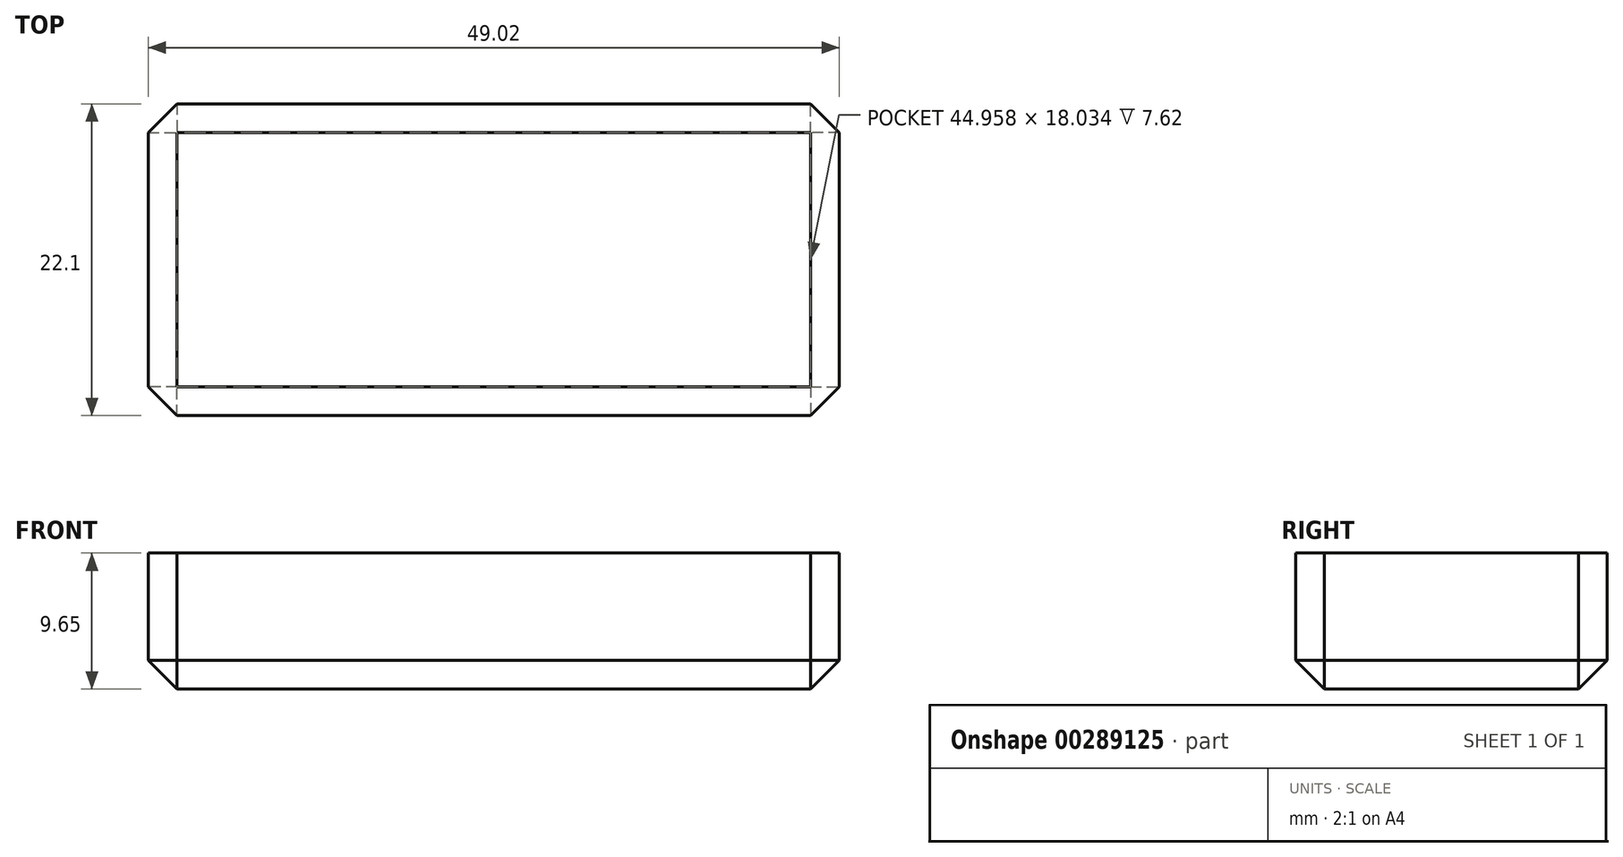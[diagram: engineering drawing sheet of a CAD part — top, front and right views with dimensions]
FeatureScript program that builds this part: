
annotation { "Feature Type Name" : "Feature", "Feature Type Description" : "" }
export const myFeature = defineFeature(function(context is Context, id is Id, definition is map)
    precondition{}
    {
        {
            var Q0;
            Q0=qCreatedBy(makeId("Top.planeOp"),FACE);
            var sketch = newSketch(context, id + "F0", { "sketchPlane" : qUnion([Q0])});
            skLineSegment(sketch, "E0.bottom", {"start": v(-24.51, 11.05) * mm, "end": v(24.51, 11.05) * mm});
            skLineSegment(sketch, "E0.top", {"start": v(-24.51, -11.05) * mm, "end": v(24.51, -11.05) * mm});
            skLineSegment(sketch, "E0.left", {"start": v(-24.51, 11.05) * mm, "end": v(-24.51, -11.05) * mm});
            skLineSegment(sketch, "E0.right", {"start": v(24.51, 11.05) * mm, "end": v(24.51, -11.05) * mm});
            skLineSegment(sketch, "E1", {"start": v(0, 0) * mm, "end": v(0, 11.05) * mm, "construction": true});
            skLineSegment(sketch, "E2", {"start": v(0, 0) * mm, "end": v(0, -11.05) * mm, "construction": true});
            skLineSegment(sketch, "E3", {"start": v(0, 0) * mm, "end": v(-24.51, 0) * mm, "construction": true});
            skPoint(sketch, "E3.endSnap0", {"position": v(-24.51, 0) * mm});
            skLineSegment(sketch, "E4", {"start": v(0, 0) * mm, "end": v(24.51, 0) * mm, "construction": true});
            skSolve(sketch);
        }
        {
            var Q0;
            Q0=makeQuery(id+"F0.imprint","IMPRINT",FACE,{"disambiguationData":[TD([[makeQuery(id+"F0.imprint","IMPRINT",EDGE,{"derivedFrom":sQuery(id+"F0.wireOp",EDGE,"E0.bottom")}),-1.0]])]});
            extrude(context, id + "F1", {"entities" : qUnion([Q0]), "depth" : 9.65 * mm});
        }
        {
            var Q0;
            Q0=makeQuery(id+"F1.opExtrude","CAP_FACE",FACE,{"disambiguationData":[OSD([sQuery(id+"F0.wireOp",EDGE,"E0.bottom"),sQuery(id+"F0.wireOp",EDGE,"E0.top"),sQuery(id+"F0.wireOp",EDGE,"E0.left"),sQuery(id+"F0.wireOp",EDGE,"E0.right")])],"isStart":false});
            var sketch = newSketch(context, id + "F2", { "sketchPlane" : qUnion([Q0])});
            skLineSegment(sketch, "E5.bottom", {"start": v(-22.48, 9.02) * mm, "end": v(22.48, 9.02) * mm});
            skLineSegment(sketch, "E5.top", {"start": v(-22.48, -9.02) * mm, "end": v(22.48, -9.02) * mm});
            skLineSegment(sketch, "E5.left", {"start": v(-22.48, 9.02) * mm, "end": v(-22.48, 4.29) * mm});
            skLineSegment(sketch, "E5.right", {"start": v(22.48, 9.02) * mm, "end": v(22.48, -9.02) * mm});
            skLineSegment(sketch, "E6", {"start": v(-22.48, 0) * mm, "end": v(-24.51, 0) * mm, "construction": true});
            skLineSegment(sketch, "E7", {"start": v(22.48, 0) * mm, "end": v(24.51, 0) * mm, "construction": true});
            skPoint(sketch, "E7.startSnap0", {"position": v(22.48, 0) * mm});
            skPoint(sketch, "E7.endSnap0", {"position": v(22.48, 0) * mm});
            skLineSegment(sketch, "E8", {"start": v(0, 9.02) * mm, "end": v(0, 11.05) * mm, "construction": true});
            skLineSegment(sketch, "E9", {"start": v(0, -9.02) * mm, "end": v(0, -11.05) * mm, "construction": true});
            skLineSegment(sketch, "E10.trimOffspring", {"start": v(-22.48, -4.29) * mm, "end": v(-22.48, -9.02) * mm});
            skLineSegment(sketch, "E11", {"start": v(-22.48, 4.29) * mm, "end": v(-22.48, -4.29) * mm});
            skSolve(sketch);
        }
        {
            var Q0;
            Q0=qSketchRegion(id+"F2",true);
            extrude(context, id + "F3", {"entities" : qUnion([Q0]), "operationType" : NewBodyOperationType.REMOVE, "oppositeDirection" : true, "depth" : 7.62 * mm});
        }
        {
            var Q0;
            Q0=makeQuery(id+"F1.opExtrude","CAP_EDGE",EDGE,{"disambiguationData":[OSD([sQuery(id+"F0.wireOp",EDGE,"E0.top")])],"isStart":true});
            var Q1;
            Q1=makeQuery(id+"F1.opExtrude","CAP_EDGE",EDGE,{"disambiguationData":[OSD([sQuery(id+"F0.wireOp",EDGE,"E0.right")])],"isStart":true});
            var Q2;
            Q2=makeQuery(id+"F1.opExtrude","SWEPT_EDGE",EDGE,{"disambiguationData":[OSD([sQuery(id+"F0.wireOp",EDGE,"E0.top"),sQuery(id+"F0.wireOp",EDGE,"E0.right")])]});
            var Q3;
            Q3=makeQuery(id+"F1.opExtrude","SWEPT_EDGE",EDGE,{"disambiguationData":[OSD([sQuery(id+"F0.wireOp",EDGE,"E0.bottom"),sQuery(id+"F0.wireOp",EDGE,"E0.right")])]});
            var Q4;
            Q4=makeQuery(id+"F1.opExtrude","CAP_EDGE",EDGE,{"disambiguationData":[OSD([sQuery(id+"F0.wireOp",EDGE,"E0.left")])],"isStart":true});
            var Q5;
            Q5=makeQuery(id+"F1.opExtrude","CAP_EDGE",EDGE,{"disambiguationData":[OSD([sQuery(id+"F0.wireOp",EDGE,"E0.bottom")])],"isStart":true});
            var Q6;
            Q6=makeQuery(id+"F1.opExtrude","SWEPT_EDGE",EDGE,{"disambiguationData":[OSD([sQuery(id+"F0.wireOp",EDGE,"E0.top"),sQuery(id+"F0.wireOp",EDGE,"E0.left")])]});
            var Q7;
            Q7=makeQuery(id+"F1.opExtrude","SWEPT_EDGE",EDGE,{"disambiguationData":[OSD([sQuery(id+"F0.wireOp",EDGE,"E0.bottom"),sQuery(id+"F0.wireOp",EDGE,"E0.left")])]});
            chamfer(context, id + "F4", {"entities" : qUnion([Q0, Q1, Q2, Q3, Q4, Q5, Q6, Q7]), "width" : 2.03 * mm, "tangentPropagation" : true});
        }
    });
